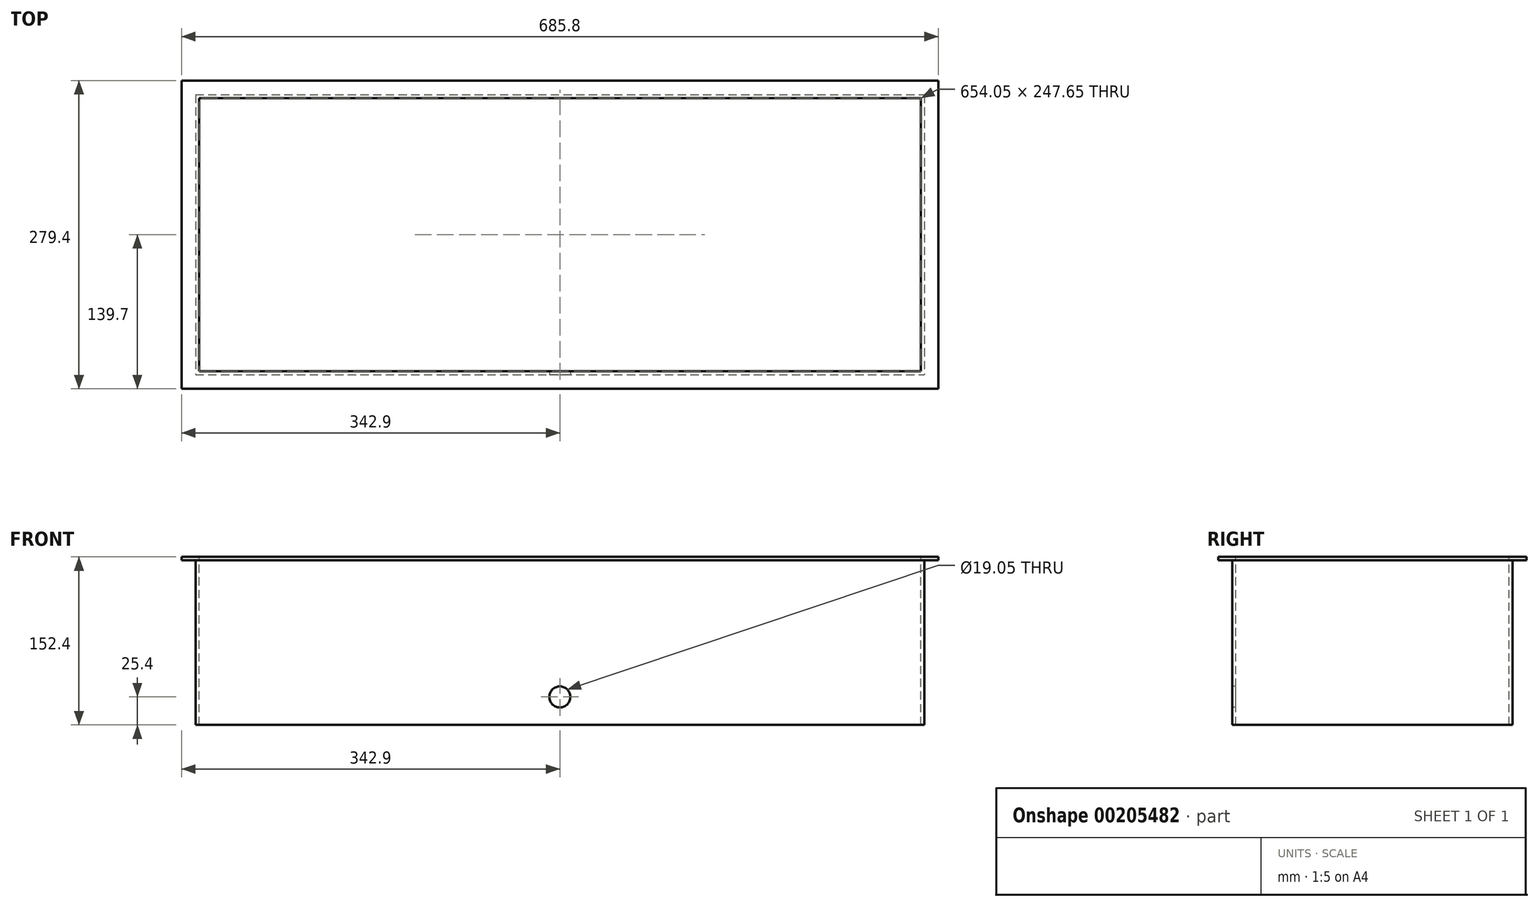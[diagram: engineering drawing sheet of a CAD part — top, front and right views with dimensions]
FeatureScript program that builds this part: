
annotation { "Feature Type Name" : "Feature", "Feature Type Description" : "" }
export const myFeature = defineFeature(function(context is Context, id is Id, definition is map)
    precondition{}
    {
        {
            var Q0;
            Q0=qCreatedBy(makeId("Top.planeOp"),FACE);
            var sketch = newSketch(context, id + "F0", { "sketchPlane" : qUnion([Q0])});
            skLineSegment(sketch, "E0.bottom", {"start": v(-330.2, 127) * mm, "end": v(330.2, 127) * mm});
            skLineSegment(sketch, "E0.top", {"start": v(-330.2, -127) * mm, "end": v(330.2, -127) * mm});
            skLineSegment(sketch, "E0.left", {"start": v(-330.2, 127) * mm, "end": v(-330.2, -127) * mm});
            skLineSegment(sketch, "E0.right", {"start": v(330.2, 127) * mm, "end": v(330.2, -127) * mm});
            skLineSegment(sketch, "E1", {"start": v(-330.2, 0) * mm, "end": v(330.2, 0) * mm, "construction": true});
            skLineSegment(sketch, "E2", {"start": v(0, 127) * mm, "end": v(0, -127) * mm, "construction": true});
            skSolve(sketch);
        }
        {
            var Q0;
            Q0=makeQuery(id+"F0.imprint","IMPRINT",FACE,{"disambiguationData":[TD([[makeQuery(id+"F0.imprint","IMPRINT",EDGE,{"derivedFrom":sQuery(id+"F0.wireOp",EDGE,"E0.bottom")}),-1.0]])]});
            extrude(context, id + "F1", {"entities" : qUnion([Q0]), "depth" : 152.4 * mm});
        }
        {
            var Q0;
            Q0=makeQuery(id+"F1.opExtrude","CAP_FACE",FACE,{"disambiguationData":[OSD([sQuery(id+"F0.wireOp",EDGE,"E0.bottom"),sQuery(id+"F0.wireOp",EDGE,"E0.top"),sQuery(id+"F0.wireOp",EDGE,"E0.left"),sQuery(id+"F0.wireOp",EDGE,"E0.right")])],"isStart":false});
            var sketch = newSketch(context, id + "F2", { "sketchPlane" : qUnion([Q0])});
            skLineSegment(sketch, "E3.0", {"start": v(-327.03, 123.83) * mm, "end": v(-327.03, -123.83) * mm});
            skLineSegment(sketch, "E3.1", {"start": v(327.03, 123.83) * mm, "end": v(-327.03, 123.83) * mm});
            skLineSegment(sketch, "E3.2", {"start": v(327.03, -123.83) * mm, "end": v(327.03, 123.83) * mm});
            skLineSegment(sketch, "E3.3", {"start": v(-327.03, -123.83) * mm, "end": v(327.03, -123.83) * mm});
            skSolve(sketch);
        }
        {
            var Q0;
            Q0=makeQuery(id+"F2.imprint","IMPRINT",FACE,{"disambiguationData":[TD([[makeQuery(id+"F2.imprint","IMPRINT",EDGE,{"derivedFrom":sQuery(id+"F2.wireOp",EDGE,"E3.0")}),1.0]])]});
            extrude(context, id + "F3", {"entities" : qUnion([Q0]), "operationType" : NewBodyOperationType.REMOVE, "endBound" : BoundingType.THROUGH_ALL, "oppositeDirection" : true, "depth" : 25.4 * mm});
        }
        {
            var Q0;
            Q0=makeQuery(id+"F1.opExtrude","CAP_FACE",FACE,{"disambiguationData":[OSD([sQuery(id+"F0.wireOp",EDGE,"E0.bottom"),sQuery(id+"F0.wireOp",EDGE,"E0.top"),sQuery(id+"F0.wireOp",EDGE,"E0.left"),sQuery(id+"F0.wireOp",EDGE,"E0.right")])],"isStart":false});
            var sketch = newSketch(context, id + "F4", { "sketchPlane" : qUnion([Q0])});
            skLineSegment(sketch, "E4.0", {"start": v(-342.9, 139.7) * mm, "end": v(-342.9, -139.7) * mm});
            skLineSegment(sketch, "E4.1", {"start": v(342.9, 139.7) * mm, "end": v(-342.9, 139.7) * mm});
            skLineSegment(sketch, "E4.2", {"start": v(342.9, -139.7) * mm, "end": v(342.9, 139.7) * mm});
            skLineSegment(sketch, "E4.3", {"start": v(-342.9, -139.7) * mm, "end": v(342.9, -139.7) * mm});
            skSolve(sketch);
        }
        {
            var Q0;
            Q0=makeQuery(id+"F4.imprint","IMPRINT",FACE,{"disambiguationData":[TD([[makeQuery(id+"F4.imprint","IMPRINT",EDGE,{"derivedFrom":sQuery(id+"F4.wireOp",EDGE,"E4.0")}),1.0]])]});
            extrude(context, id + "F5", {"entities" : qUnion([Q0]), "operationType" : NewBodyOperationType.ADD, "oppositeDirection" : true, "depth" : 3.17 * mm});
        }
        {
            var Q0;
            Q0=makeQuery(id+"F1.opExtrude","SWEPT_FACE",FACE,{"disambiguationData":[OSD([sQuery(id+"F0.wireOp",EDGE,"E0.top")])]});
            var sketch = newSketch(context, id + "F6", { "sketchPlane" : qUnion([Q0])});
            skCircle(sketch, "E5", {"center": v(0, 25.4) * mm, "radius": 9.53 * mm});
            skSolve(sketch);
        }
        {
            var Q0;
            Q0=makeQuery(id+"F6.imprint","IMPRINT",FACE,{"disambiguationData":[TD([[makeQuery(id+"F6.imprint","IMPRINT",EDGE,{"derivedFrom":sQuery(id+"F6.wireOp",EDGE,"E5")}),1.0]])]});
            extrude(context, id + "F7", {"entities" : qUnion([Q0]), "operationType" : NewBodyOperationType.REMOVE, "endBound" : BoundingType.UP_TO_NEXT, "oppositeDirection" : true, "depth" : 25.4 * mm});
        }
    });
